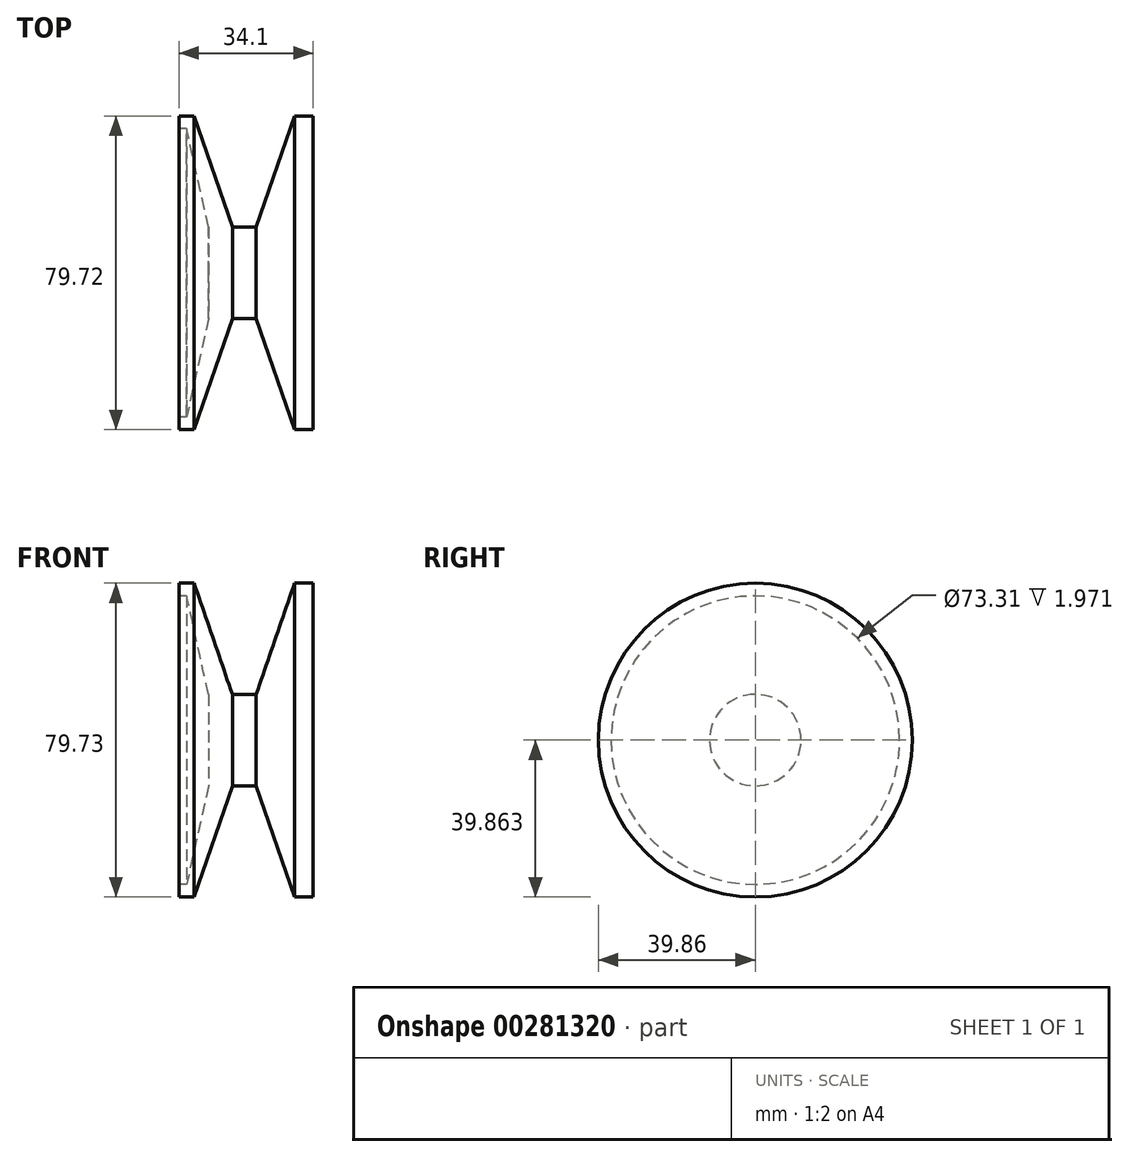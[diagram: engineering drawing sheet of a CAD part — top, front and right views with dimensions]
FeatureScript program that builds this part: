
annotation { "Feature Type Name" : "Feature", "Feature Type Description" : "" }
export const myFeature = defineFeature(function(context is Context, id is Id, definition is map)
    precondition{}
    {
        {
            var Q0;
            Q0=qCreatedBy(makeId("Front.planeOp"),FACE);
            var sketch = newSketch(context, id + "F0", { "sketchPlane" : qUnion([Q0])});
            skLineSegment(sketch, "E0", {"start": v(0, 0) * mm, "end": v(-2.8, 0) * mm});
            skLineSegment(sketch, "E1", {"start": v(0, 0) * mm, "end": v(3.3, 0) * mm});
            skLineSegment(sketch, "E2", {"start": v(-2.8, 0) * mm, "end": v(-12.52, 28.24) * mm});
            skLineSegment(sketch, "E3", {"start": v(3.3, 0) * mm, "end": v(13.02, 28.24) * mm});
            skLineSegment(sketch, "E4", {"start": v(-12.52, 28.24) * mm, "end": v(-16.36, 28.24) * mm});
            skLineSegment(sketch, "E5", {"start": v(-16.36, 28.24) * mm, "end": v(-16.36, 25.03) * mm});
            skLineSegment(sketch, "E6", {"start": v(-16.36, 25.03) * mm, "end": v(-14.39, 25.03) * mm});
            skLineSegment(sketch, "E7", {"start": v(-14.39, 25.03) * mm, "end": v(-8.87, 0) * mm});
            skLineSegment(sketch, "E8", {"start": v(-8.87, 0) * mm, "end": v(-8.87, -11.63) * mm});
            skLineSegment(sketch, "E9", {"start": v(13.02, 28.24) * mm, "end": v(17.74, 28.24) * mm});
            skLineSegment(sketch, "E10", {"start": v(17.74, 28.24) * mm, "end": v(17.74, -11.63) * mm});
            skLineSegment(sketch, "E11", {"start": v(-8.87, -11.63) * mm, "end": v(17.74, -11.63) * mm});
            skSolve(sketch);
        }
        {
            var Q0;
            Q0=makeQuery(id+"F0.imprint","IMPRINT",FACE,{"disambiguationData":[TD([[makeQuery(id+"F0.imprint","IMPRINT",EDGE,{"derivedFrom":sQuery(id+"F0.wireOp",EDGE,"E0")}),1.0]])]});
            var Q1;
            Q1=sQuery(id+"F0.wireOp",EDGE,"E11");
            revolve(context, id + "F1", {"entities" : qUnion([Q0]), "axis" : qUnion([Q1]), "revolveType" : RevolveType.FULL});
        }
    });
